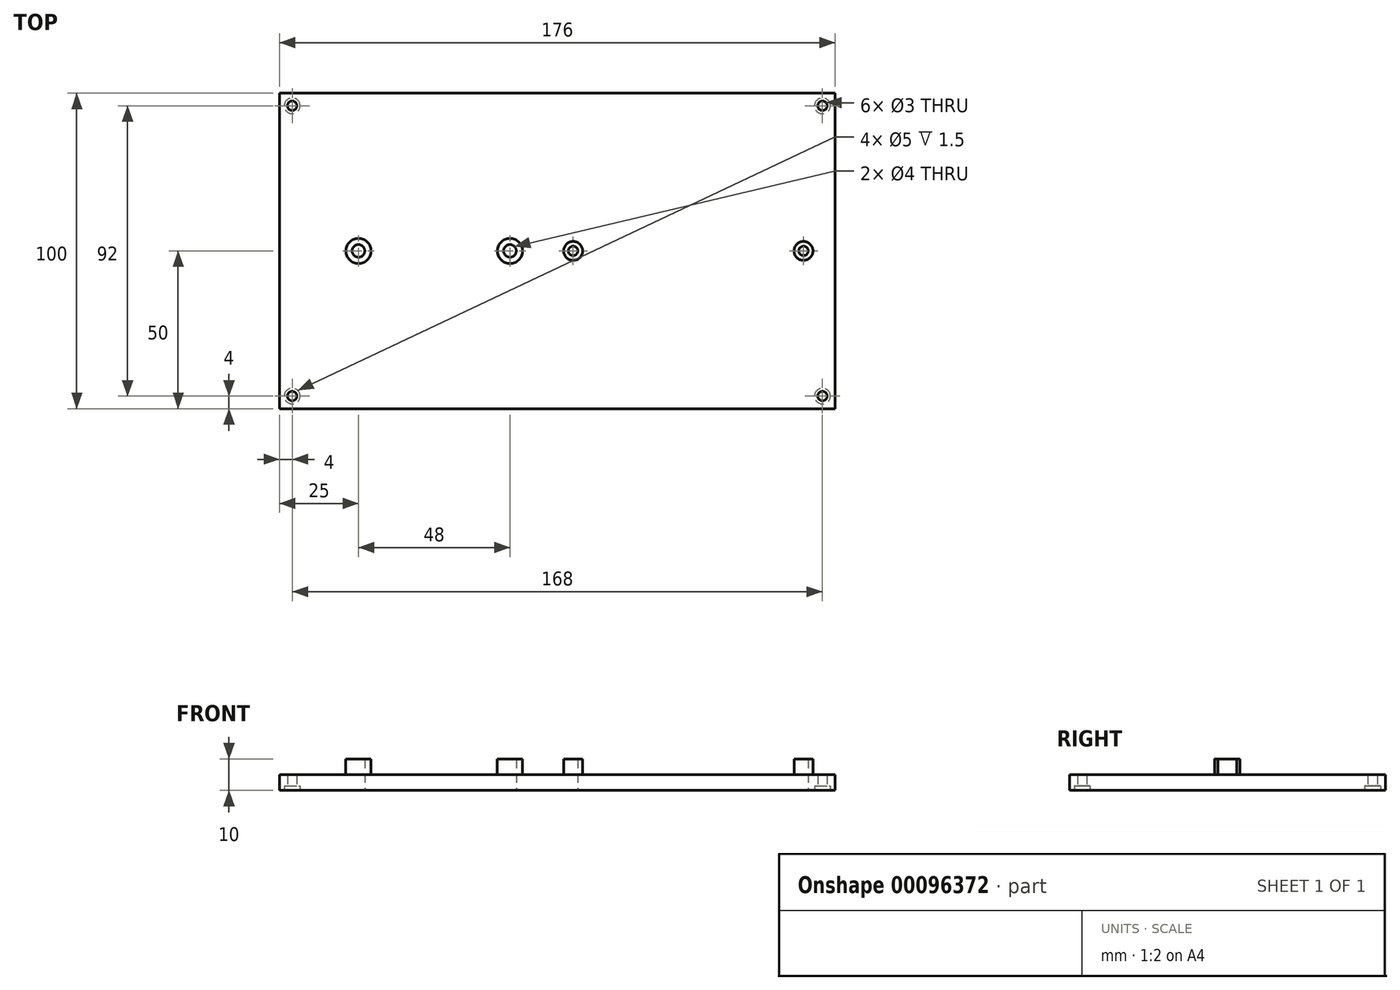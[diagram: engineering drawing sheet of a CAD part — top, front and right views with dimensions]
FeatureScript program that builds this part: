
annotation { "Feature Type Name" : "Feature", "Feature Type Description" : "" }
export const myFeature = defineFeature(function(context is Context, id is Id, definition is map)
    precondition{}
    {
        {
            var Q0;
            Q0=qCreatedBy(makeId("Top.planeOp"),FACE);
            var sketch = newSketch(context, id + "F0", { "sketchPlane" : qUnion([Q0])});
            skLineSegment(sketch, "E0.bottom", {"start": v(-88, -50) * mm, "end": v(88, -50) * mm});
            skLineSegment(sketch, "E0.top", {"start": v(-88, 50) * mm, "end": v(88, 50) * mm});
            skLineSegment(sketch, "E0.left", {"start": v(-88, -50) * mm, "end": v(-88, 50) * mm});
            skLineSegment(sketch, "E0.right", {"start": v(88, -50) * mm, "end": v(88, 50) * mm});
            skPoint(sketch, "E0.middle", {"position": v(0, 0) * mm});
            skCircle(sketch, "E1", {"center": v(-63, 0) * mm, "radius": 2 * mm});
            skCircle(sketch, "E2", {"center": v(-63, 0) * mm, "radius": 4 * mm});
            skCircle(sketch, "E3", {"center": v(-15, 0) * mm, "radius": 2 * mm});
            skCircle(sketch, "E4", {"center": v(-15, 0) * mm, "radius": 4 * mm});
            skCircle(sketch, "E5", {"center": v(5, 0) * mm, "radius": 1.5 * mm});
            skCircle(sketch, "E6", {"center": v(78, 0) * mm, "radius": 1.5 * mm});
            skCircle(sketch, "E7", {"center": v(5, 0) * mm, "radius": 3 * mm});
            skCircle(sketch, "E8", {"center": v(78, 0) * mm, "radius": 3 * mm});
            skSolve(sketch);
        }
        {
            var Q0;
            Q0=makeQuery(id+"F0.imprint","IMPRINT",FACE,{"disambiguationData":[TD([[makeQuery(id+"F0.imprint","IMPRINT",EDGE,{"derivedFrom":sQuery(id+"F0.wireOp",EDGE,"E0.bottom")}),1.0]])]});
            var Q1;
            Q1 = qSketchRegion(id + "F0", true);
            extrude(context, id + "F1", {"entities" : qUnion([Q0, Q1]), "depth" : 5 * mm});
        }
        {
            var Q0;
            Q0=makeQuery(id+"F0.imprint","IMPRINT",FACE,{"disambiguationData":[TD([[makeQuery(id+"F0.imprint","IMPRINT",EDGE,{"derivedFrom":sQuery(id+"F0.wireOp",EDGE,"E1")}),-1.0]])]});
            var Q1;
            Q1=makeQuery(id+"F0.imprint","IMPRINT",FACE,{"disambiguationData":[TD([[makeQuery(id+"F0.imprint","IMPRINT",EDGE,{"derivedFrom":sQuery(id+"F0.wireOp",EDGE,"E3")}),-1.0]])]});
            var Q2;
            Q2=makeQuery(id+"F0.imprint","IMPRINT",FACE,{"disambiguationData":[TD([[makeQuery(id+"F0.imprint","IMPRINT",EDGE,{"derivedFrom":sQuery(id+"F0.wireOp",EDGE,"E5")}),-1.0]])]});
            var Q3;
            Q3=makeQuery(id+"F0.imprint","IMPRINT",FACE,{"disambiguationData":[TD([[makeQuery(id+"F0.imprint","IMPRINT",EDGE,{"derivedFrom":sQuery(id+"F0.wireOp",EDGE,"E6")}),-1.0]])]});
            extrude(context, id + "F2", {"entities" : qUnion([Q0, Q1, Q2, Q3]), "operationType" : NewBodyOperationType.ADD, "depth" : 10 * mm});
        }
        {
            var Q0;
            {var subQ0=sQuery(id+"F0.wireOp",EDGE,"E8");var subQ1=sQuery(id+"F0.wireOp",EDGE,"E7");var subQ2=sQuery(id+"F0.wireOp",EDGE,"E4");var subQ3=sQuery(id+"F0.wireOp",EDGE,"E2");Q0=makeQuery(id+"F2.boolean.opBoolean","MERGE",FACE,{"derivedFrom":[makeQuery(id+"F1.opExtrude","CAP_FACE",FACE,{"disambiguationData":[OSD([sQuery(id+"F0.wireOp",EDGE,"E0.bottom"),sQuery(id+"F0.wireOp",EDGE,"E0.top"),sQuery(id+"F0.wireOp",EDGE,"E0.left"),sQuery(id+"F0.wireOp",EDGE,"E0.right"),subQ3,subQ2,subQ1,subQ0])],"isStart":true}),makeQuery(id+"F2.opExtrude","CAP_FACE",FACE,{"disambiguationData":[OSD([sQuery(id+"F0.wireOp",EDGE,"E1"),subQ3])],"isStart":true}),makeQuery(id+"F2.opExtrude","CAP_FACE",FACE,{"disambiguationData":[OSD([sQuery(id+"F0.wireOp",EDGE,"E3"),subQ2])],"isStart":true}),makeQuery(id+"F2.opExtrude","CAP_FACE",FACE,{"disambiguationData":[OSD([sQuery(id+"F0.wireOp",EDGE,"E5"),subQ1])],"isStart":true}),makeQuery(id+"F2.opExtrude","CAP_FACE",FACE,{"disambiguationData":[OSD([sQuery(id+"F0.wireOp",EDGE,"E6"),subQ0])],"isStart":true})]});}
            var sketch = newSketch(context, id + "F3", { "sketchPlane" : qUnion([Q0])});
            skSolve(sketch);
        }
        {
            var Q0;
            Q0=makeQuery(id+"F3.imprint","IMPRINT",FACE,{"disambiguationData":[TD([[makeQuery(id+"F3.imprint","IMPRINT",EDGE,{"derivedFrom":makeQuery(id+"F1.opExtrude","CAP_EDGE",EDGE,{"disambiguationData":[OSD([sQuery(id+"F0.wireOp",EDGE,"E0.bottom")])],"isStart":true})}),-1.0]])]});
            var sketch = newSketch(context, id + "F4", { "sketchPlane" : qUnion([Q0])});
            skCircle(sketch, "E9", {"center": v(-84, 46) * mm, "radius": 1.5 * mm});
            skCircle(sketch, "E10", {"center": v(-84, 46) * mm, "radius": 2.5 * mm});
            skCircle(sketch, "E11", {"center": v(-84, -46) * mm, "radius": 1.5 * mm});
            skCircle(sketch, "E12", {"center": v(-84, -46) * mm, "radius": 2.5 * mm});
            skCircle(sketch, "E13", {"center": v(84, -46) * mm, "radius": 1.5 * mm});
            skCircle(sketch, "E14", {"center": v(84, -46) * mm, "radius": 2.5 * mm});
            skCircle(sketch, "E15", {"center": v(84, 46) * mm, "radius": 1.5 * mm});
            skCircle(sketch, "E16", {"center": v(84, 46) * mm, "radius": 2.5 * mm});
            skSolve(sketch);
        }
        {
            var Q0;
            Q0=makeQuery(id+"F4.imprint","IMPRINT",FACE,{"disambiguationData":[TD([[makeQuery(id+"F4.imprint","IMPRINT",EDGE,{"derivedFrom":sQuery(id+"F4.wireOp",EDGE,"E9")}),1.0]])]});
            var Q1;
            Q1=makeQuery(id+"F4.imprint","IMPRINT",FACE,{"disambiguationData":[TD([[makeQuery(id+"F4.imprint","IMPRINT",EDGE,{"derivedFrom":sQuery(id+"F4.wireOp",EDGE,"E11")}),1.0]])]});
            var Q2;
            Q2=makeQuery(id+"F4.imprint","IMPRINT",FACE,{"disambiguationData":[TD([[makeQuery(id+"F4.imprint","IMPRINT",EDGE,{"derivedFrom":sQuery(id+"F4.wireOp",EDGE,"E15")}),1.0]])]});
            var Q3;
            Q3=makeQuery(id+"F4.imprint","IMPRINT",FACE,{"disambiguationData":[TD([[makeQuery(id+"F4.imprint","IMPRINT",EDGE,{"derivedFrom":sQuery(id+"F4.wireOp",EDGE,"E13")}),1.0]])]});
            extrude(context, id + "F5", {"entities" : qUnion([Q0, Q1, Q2, Q3]), "operationType" : NewBodyOperationType.REMOVE, "endBound" : BoundingType.THROUGH_ALL, "oppositeDirection" : true, "depth" : 25 * mm});
        }
        {
            var Q0;
            Q0=makeQuery(id+"F4.imprint","IMPRINT",FACE,{"disambiguationData":[TD([[makeQuery(id+"F4.imprint","IMPRINT",EDGE,{"derivedFrom":sQuery(id+"F4.wireOp",EDGE,"E13")}),-1.0]])]});
            var Q1;
            Q1=makeQuery(id+"F4.imprint","IMPRINT",FACE,{"disambiguationData":[TD([[makeQuery(id+"F4.imprint","IMPRINT",EDGE,{"derivedFrom":sQuery(id+"F4.wireOp",EDGE,"E15")}),-1.0]])]});
            var Q2;
            Q2=makeQuery(id+"F4.imprint","IMPRINT",FACE,{"disambiguationData":[TD([[makeQuery(id+"F4.imprint","IMPRINT",EDGE,{"derivedFrom":sQuery(id+"F4.wireOp",EDGE,"E9")}),-1.0]])]});
            var Q3;
            Q3=makeQuery(id+"F4.imprint","IMPRINT",FACE,{"disambiguationData":[TD([[makeQuery(id+"F4.imprint","IMPRINT",EDGE,{"derivedFrom":sQuery(id+"F4.wireOp",EDGE,"E11")}),-1.0]])]});
            extrude(context, id + "F6", {"entities" : qUnion([Q0, Q1, Q2, Q3]), "operationType" : NewBodyOperationType.REMOVE, "oppositeDirection" : true, "depth" : 1.5 * mm});
        }
    });
